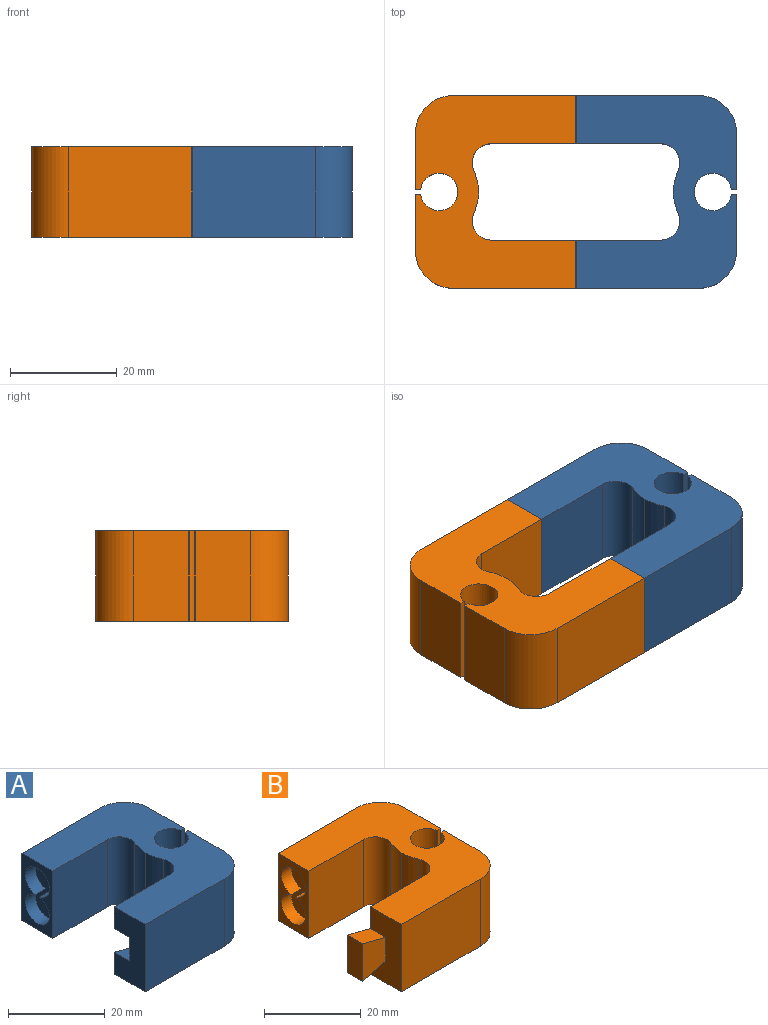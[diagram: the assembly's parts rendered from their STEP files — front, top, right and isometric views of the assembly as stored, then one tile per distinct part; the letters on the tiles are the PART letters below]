
ASSEMBLY  parts=2 mates=1
PART A: 28 faces, bbox 30x36x17 mm
  f0: plane 17x15.9mm, normal (0,1,0), area 217.8mm2, adj f1,f13,f14,f16,f24,f25,f26
  f1: plane 17x9mm, normal (-1,0,0), area 126mm2, adj f0,f6,f13,f14,f24,f25,f27
  f2: plane 17x9mm, normal (-1,0,0), area 76.1mm2, adj f3,f12,f13,f14,f19,f20
  f3: plane 17x15.9mm, normal (0,-1,0), area 270.3mm2, adj f2,f13,f14,f15
  f4: extruded ~17x4.21mm, area 73.8mm2, adj f5,f13,f14,f15
  f5: extruded ~17x4.21mm, area 73.8mm2, adj f4,f13,f14,f16
  f6: plane 23x17mm, normal (0,-1,0), area 391mm2, adj f1,f13,f14,f17
  f7: plane 17x10.4mm, normal (1,0,0), area 176.8mm2, adj f13,f14,f17,f22
  f8: plane 17x0.86mm, normal (0,1,0), area 14.6mm2, adj f9,f13,f14,f22
  f9: cylinder r=3.5mm len=17mm, axis (0,0,-1), area 356.8mm2, adj f8,f10,f13,f14
  f10: plane 17x0.86mm, normal (0,-1,0), area 14.6mm2, adj f9,f13,f14,f23
  f11: plane 17x10.4mm, normal (1,0,0), area 176.8mm2, adj f13,f14,f18,f23
  f12: plane 23x17mm, normal (0,1,0), area 391mm2, adj f2,f13,f14,f18
  f13: plane 36x30mm, normal (0,0,1), area 683.1mm2, adj f0,f1,f2,f3,f4,f5,f6,f7
  f14: plane 36x30mm, normal (0,0,-1), area 683.1mm2, adj f0,f1,f2,f3,f4,f5,f6,f7
  f15: cylinder r=3.5mm len=17mm, axis (0,0,-1), area 116mm2, adj f3,f4,f13,f14
  f16: cylinder r=3.5mm len=17mm, axis (0,0,-1), area 116mm2, adj f0,f5,f13,f14
  f17: cylinder r=7mm len=17mm, axis (0,0,-1), area 186.9mm2, adj f6,f7,f13,f14
  f18: cylinder r=7mm len=17mm, axis (0,0,1), area 186.9mm2, adj f11,f12,f13,f14
  f19: cylinder r=3.5mm len=7mm, axis (-1,0,0), area 62.4mm2, adj f2,f20,f21
  f20: cylinder r=3.5mm len=7mm, axis (-1,0,0), area 62.4mm2, adj f2,f19,f21
  f21: plane 13.9x7mm, normal (-1,0,0), area 76.9mm2, adj f19,f20
  f22: cylinder r=0.1mm len=17mm, axis (0,0,1), area 2.7mm2, adj f7,f8,f13,f14
  f23: cylinder r=0.1mm len=17mm, axis (0,0,-1), area 2.7mm2, adj f10,f11,f13,f14
  f24: plane 6.78x4.5mm, normal (0.25,0,0.97), area 31.5mm2, adj f0,f1,f26,f27
  f25: plane 6.78x4.5mm, normal (0.25,0,-0.97), area 31.5mm2, adj f0,f1,f26,f27
  f26: plane 9.5x4.5mm, normal (-1,0,0), area 42.7mm2, adj f0,f24,f25,f27
  f27: plane 9.5x6.78mm, normal (0,1,0), area 52.5mm2, adj f1,f24,f25,f26
PART B: 28 faces, bbox 36.8x36x17 mm
  f0: plane 17x9mm, normal (-1,0,0), area 76.1mm2, adj f1,f12,f13,f14,f19,f20
  f1: plane 17x15.9mm, normal (0,-1,0), area 270.3mm2, adj f0,f13,f14,f15
  f2: extruded ~17x4.21mm, area 73.8mm2, adj f3,f13,f14,f15
  f3: extruded ~17x4.21mm, area 73.8mm2, adj f2,f13,f14,f16
  f4: plane 22.68x17mm, normal (0,1,0), area 322.9mm2, adj f5,f13,f14,f16,f24,f25,f26
  f5: plane 17x9mm, normal (-1,0,0), area 126mm2, adj f4,f6,f13,f14,f24,f26,f27
  f6: plane 23x17mm, normal (0,-1,0), area 391mm2, adj f5,f13,f14,f17
  f7: plane 17x10.4mm, normal (1,0,0), area 176.8mm2, adj f13,f14,f17,f22
  f8: plane 17x0.86mm, normal (0,1,0), area 14.6mm2, adj f9,f13,f14,f22
  f9: cylinder r=3.5mm len=17mm, axis (0,0,-1), area 356.8mm2, adj f8,f10,f13,f14
  f10: plane 17x0.86mm, normal (0,-1,0), area 14.6mm2, adj f9,f13,f14,f23
  f11: plane 17x10.4mm, normal (1,0,0), area 176.8mm2, adj f13,f14,f18,f23
  f12: plane 23x17mm, normal (0,1,0), area 391mm2, adj f0,f13,f14,f18
  f13: plane 36x30mm, normal (0,0,1), area 683.1mm2, adj f0,f1,f2,f3,f4,f5,f6,f7
  f14: plane 36x30mm, normal (0,0,-1), area 683.1mm2, adj f0,f1,f2,f3,f4,f5,f6,f7
  f15: cylinder r=3.5mm len=17mm, axis (0,0,-1), area 116mm2, adj f1,f2,f13,f14
  f16: cylinder r=3.5mm len=17mm, axis (0,0,-1), area 116mm2, adj f3,f4,f13,f14
  f17: cylinder r=7mm len=17mm, axis (0,0,-1), area 186.9mm2, adj f6,f7,f13,f14
  f18: cylinder r=7mm len=17mm, axis (0,0,1), area 186.9mm2, adj f11,f12,f13,f14
  f19: cylinder r=3.5mm len=7mm, axis (-1,0,0), area 62.4mm2, adj f0,f20,f21
  f20: cylinder r=3.5mm len=7mm, axis (-1,0,0), area 62.4mm2, adj f0,f19,f21
  f21: plane 13.9x7mm, normal (-1,0,0), area 76.9mm2, adj f19,f20
  f22: cylinder r=0.1mm len=17mm, axis (0,0,1), area 2.7mm2, adj f7,f8,f13,f14
  f23: cylinder r=0.1mm len=17mm, axis (0,0,-1), area 2.7mm2, adj f10,f11,f13,f14
  f24: plane 6.78x4.5mm, normal (0.25,0,-0.97), area 31.5mm2, adj f4,f5,f25,f27
  f25: plane 9.5x4.5mm, normal (-1,0,0), area 42.7mm2, adj f4,f24,f26,f27
  f26: plane 6.78x4.5mm, normal (0.25,0,0.97), area 31.5mm2, adj f4,f5,f25,f27
  f27: plane 9.5x6.78mm, normal (0,-1,0), area 52.5mm2, adj f5,f24,f25,f26
PLACE A t=(-29.01,-0.52,0.07)mm
PLACE B rot(axis=(0,-1,0),180deg) t=(-35.13,-0.52,17.07)mm
MATE slider A.f27 <-> B.f27  axis (0,1,0) through (-28.42,-14.02,8.57)mm
